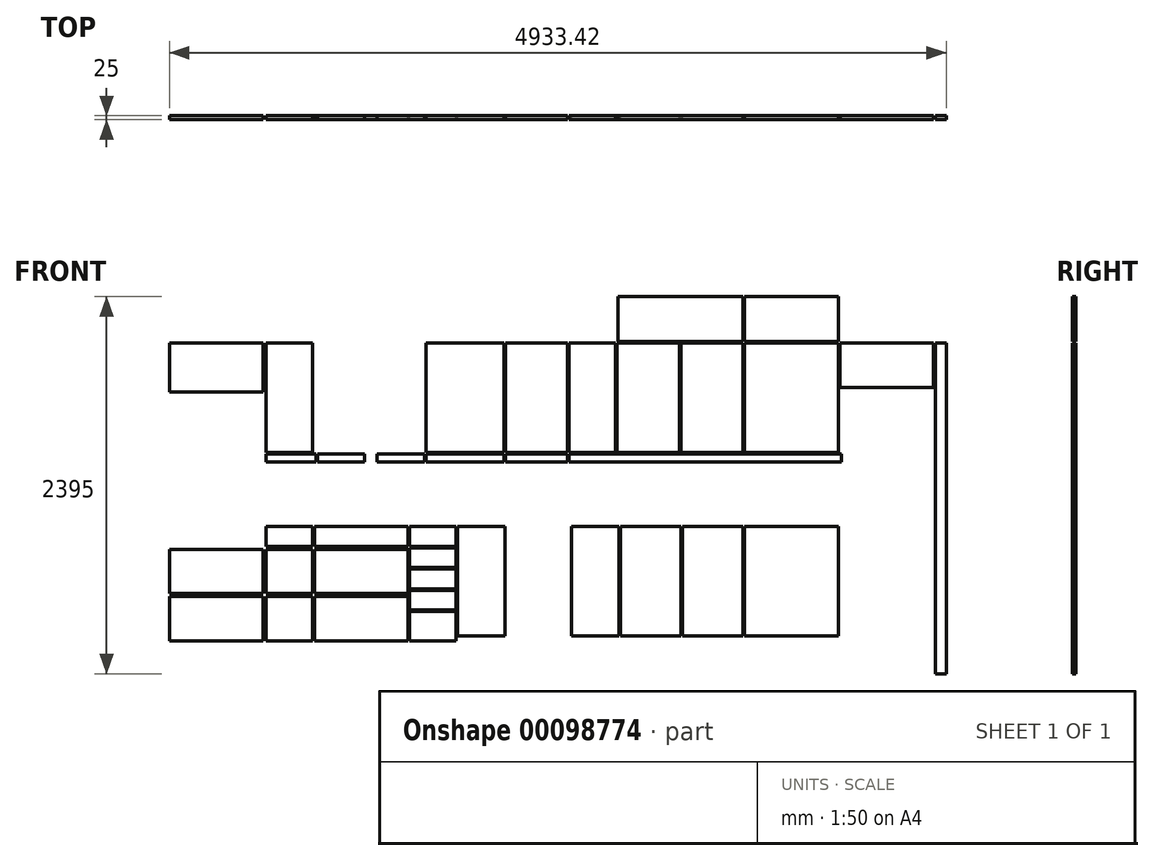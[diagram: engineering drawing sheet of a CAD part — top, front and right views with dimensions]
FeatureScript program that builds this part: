
annotation { "Feature Type Name" : "Feature", "Feature Type Description" : "" }
export const myFeature = defineFeature(function(context is Context, id is Id, definition is map)
    precondition{}
    {
        {
            var Q0;
            Q0=qCreatedBy(makeId("Front.planeOp"),FACE);
            var sketch = newSketch(context, id + "F0", { "sketchPlane" : qUnion([Q0])});
            skLineSegment(sketch, "E0.bottom", {"start": v(-883.14, -290.46) * mm, "end": v(-288.14, -290.46) * mm});
            skLineSegment(sketch, "E0.top", {"start": v(-883.14, -600.46) * mm, "end": v(-288.14, -600.46) * mm});
            skLineSegment(sketch, "E0.left", {"start": v(-883.14, -290.46) * mm, "end": v(-883.14, -600.46) * mm});
            skLineSegment(sketch, "E0.right", {"start": v(-288.14, -290.46) * mm, "end": v(-288.14, -600.46) * mm});
            skLineSegment(sketch, "E1.bottom", {"start": v(-883.14, -1600.46) * mm, "end": v(-288.14, -1600.46) * mm});
            skLineSegment(sketch, "E1.top", {"start": v(-883.14, -1880.46) * mm, "end": v(-288.14, -1880.46) * mm});
            skLineSegment(sketch, "E1.left", {"start": v(-883.14, -1600.46) * mm, "end": v(-883.14, -1880.46) * mm});
            skLineSegment(sketch, "E1.right", {"start": v(-288.14, -1600.46) * mm, "end": v(-288.14, -1880.46) * mm});
            skLineSegment(sketch, "E2.bottom", {"start": v(-883.14, -1900.46) * mm, "end": v(-288.14, -1900.46) * mm});
            skLineSegment(sketch, "E2.top", {"start": v(-883.14, -2180.46) * mm, "end": v(-288.14, -2180.46) * mm});
            skLineSegment(sketch, "E2.left", {"start": v(-883.14, -1900.46) * mm, "end": v(-883.14, -2180.46) * mm});
            skLineSegment(sketch, "E2.right", {"start": v(-288.14, -1900.46) * mm, "end": v(-288.14, -2180.46) * mm});
            skLineSegment(sketch, "E3.bottom", {"start": v(-268.14, -290.46) * mm, "end": v(26.86, -290.46) * mm});
            skLineSegment(sketch, "E3.top", {"start": v(-268.14, -985.46) * mm, "end": v(26.86, -985.46) * mm});
            skLineSegment(sketch, "E3.left", {"start": v(-268.14, -290.46) * mm, "end": v(-268.14, -985.46) * mm});
            skLineSegment(sketch, "E3.right", {"start": v(26.86, -290.46) * mm, "end": v(26.86, -985.46) * mm});
            skPoint(sketch, "E4.oppositeSnap0", {"position": v(-585.64, -1880.46) * mm});
            skLineSegment(sketch, "E4.bottom", {"start": v(-268.14, -1600.46) * mm, "end": v(26.86, -1600.46) * mm});
            skLineSegment(sketch, "E4.top", {"start": v(-268.14, -1880.46) * mm, "end": v(26.86, -1880.46) * mm});
            skLineSegment(sketch, "E4.left", {"start": v(-268.14, -1600.46) * mm, "end": v(-268.14, -1880.46) * mm});
            skLineSegment(sketch, "E4.right", {"start": v(26.86, -1600.46) * mm, "end": v(26.86, -1880.46) * mm});
            skLineSegment(sketch, "E5.bottom", {"start": v(-268.14, -1900.46) * mm, "end": v(26.86, -1900.46) * mm});
            skLineSegment(sketch, "E5.top", {"start": v(-268.14, -2180.46) * mm, "end": v(26.86, -2180.46) * mm});
            skLineSegment(sketch, "E5.left", {"start": v(-268.14, -1900.46) * mm, "end": v(-268.14, -2180.46) * mm});
            skLineSegment(sketch, "E5.right", {"start": v(26.86, -1900.46) * mm, "end": v(26.86, -2180.46) * mm});
            skLineSegment(sketch, "E6.bottom", {"start": v(-268.14, -1580.46) * mm, "end": v(26.86, -1580.46) * mm});
            skLineSegment(sketch, "E6.top", {"start": v(-268.14, -1455.46) * mm, "end": v(26.86, -1455.46) * mm});
            skLineSegment(sketch, "E6.left", {"start": v(-268.14, -1580.46) * mm, "end": v(-268.14, -1455.46) * mm});
            skLineSegment(sketch, "E6.right", {"start": v(26.86, -1580.46) * mm, "end": v(26.86, -1455.46) * mm});
            skLineSegment(sketch, "E7.bottom", {"start": v(36.86, -1455.46) * mm, "end": v(631.86, -1455.46) * mm});
            skLineSegment(sketch, "E7.top", {"start": v(36.86, -1580.46) * mm, "end": v(631.86, -1580.46) * mm});
            skLineSegment(sketch, "E7.left", {"start": v(36.86, -1455.46) * mm, "end": v(36.86, -1580.46) * mm});
            skLineSegment(sketch, "E7.right", {"start": v(631.86, -1455.46) * mm, "end": v(631.86, -1580.46) * mm});
            skLineSegment(sketch, "E8.bottom", {"start": v(36.86, -1600.46) * mm, "end": v(631.86, -1600.46) * mm});
            skLineSegment(sketch, "E8.top", {"start": v(36.86, -1880.46) * mm, "end": v(631.86, -1880.46) * mm});
            skLineSegment(sketch, "E8.left", {"start": v(36.86, -1600.46) * mm, "end": v(36.86, -1880.46) * mm});
            skLineSegment(sketch, "E8.right", {"start": v(631.86, -1600.46) * mm, "end": v(631.86, -1880.46) * mm});
            skLineSegment(sketch, "E9.bottom", {"start": v(36.86, -1900.46) * mm, "end": v(631.86, -1900.46) * mm});
            skLineSegment(sketch, "E9.top", {"start": v(36.86, -2180.46) * mm, "end": v(631.86, -2180.46) * mm});
            skLineSegment(sketch, "E9.left", {"start": v(36.86, -1900.46) * mm, "end": v(36.86, -2180.46) * mm});
            skLineSegment(sketch, "E9.right", {"start": v(631.86, -1900.46) * mm, "end": v(631.86, -2180.46) * mm});
            skLineSegment(sketch, "E10.bottom", {"start": v(56.86, -995.46) * mm, "end": v(356.86, -995.46) * mm});
            skLineSegment(sketch, "E10.top", {"start": v(56.86, -1045.46) * mm, "end": v(356.86, -1045.46) * mm});
            skLineSegment(sketch, "E10.left", {"start": v(56.86, -995.46) * mm, "end": v(56.86, -1045.46) * mm});
            skLineSegment(sketch, "E10.right", {"start": v(356.86, -995.46) * mm, "end": v(356.86, -1045.46) * mm});
            skLineSegment(sketch, "E11.bottom", {"start": v(-268.14, -995.46) * mm, "end": v(46.86, -995.46) * mm});
            skLineSegment(sketch, "E11.top", {"start": v(-268.14, -1045.46) * mm, "end": v(46.86, -1045.46) * mm});
            skLineSegment(sketch, "E11.left", {"start": v(-268.14, -995.46) * mm, "end": v(-268.14, -1045.46) * mm});
            skLineSegment(sketch, "E11.right", {"start": v(46.86, -995.46) * mm, "end": v(46.86, -1045.46) * mm});
            skLineSegment(sketch, "E12.bottom", {"start": v(641.86, -1455.46) * mm, "end": v(936.86, -1455.46) * mm});
            skLineSegment(sketch, "E12.top", {"start": v(641.86, -1580.46) * mm, "end": v(936.86, -1580.46) * mm});
            skLineSegment(sketch, "E12.left", {"start": v(641.86, -1455.46) * mm, "end": v(641.86, -1580.46) * mm});
            skLineSegment(sketch, "E12.right", {"start": v(936.86, -1455.46) * mm, "end": v(936.86, -1580.46) * mm});
            skLineSegment(sketch, "E13.bottom", {"start": v(641.86, -1725.46) * mm, "end": v(936.86, -1725.46) * mm});
            skLineSegment(sketch, "E13.top", {"start": v(641.86, -1850.46) * mm, "end": v(936.86, -1850.46) * mm});
            skLineSegment(sketch, "E13.left", {"start": v(641.86, -1725.46) * mm, "end": v(641.86, -1850.46) * mm});
            skLineSegment(sketch, "E13.right", {"start": v(936.86, -1725.46) * mm, "end": v(936.86, -1850.46) * mm});
            skLineSegment(sketch, "E14.bottom", {"start": v(641.86, -1860.46) * mm, "end": v(936.86, -1860.46) * mm});
            skLineSegment(sketch, "E14.top", {"start": v(641.86, -1985.46) * mm, "end": v(936.86, -1985.46) * mm});
            skLineSegment(sketch, "E14.left", {"start": v(641.86, -1860.46) * mm, "end": v(641.86, -1985.46) * mm});
            skLineSegment(sketch, "E14.right", {"start": v(936.86, -1860.46) * mm, "end": v(936.86, -1985.46) * mm});
            skLineSegment(sketch, "E15.bottom", {"start": v(641.86, -1995.46) * mm, "end": v(936.86, -1995.46) * mm});
            skLineSegment(sketch, "E15.top", {"start": v(641.86, -2180.46) * mm, "end": v(936.86, -2180.46) * mm});
            skLineSegment(sketch, "E15.left", {"start": v(641.86, -1995.46) * mm, "end": v(641.86, -2180.46) * mm});
            skLineSegment(sketch, "E15.right", {"start": v(936.86, -1995.46) * mm, "end": v(936.86, -2180.46) * mm});
            skLineSegment(sketch, "E16.bottom", {"start": v(641.86, -1590.46) * mm, "end": v(936.86, -1590.46) * mm});
            skLineSegment(sketch, "E16.top", {"start": v(641.86, -1715.46) * mm, "end": v(936.86, -1715.46) * mm});
            skLineSegment(sketch, "E16.left", {"start": v(641.86, -1590.46) * mm, "end": v(641.86, -1715.46) * mm});
            skLineSegment(sketch, "E16.right", {"start": v(936.86, -1590.46) * mm, "end": v(936.86, -1715.46) * mm});
            skLineSegment(sketch, "E17.bottom", {"start": v(1240.28, -290.46) * mm, "end": v(745.28, -290.46) * mm});
            skLineSegment(sketch, "E17.top", {"start": v(1240.28, -985.46) * mm, "end": v(745.28, -985.46) * mm});
            skLineSegment(sketch, "E17.left", {"start": v(1240.28, -290.46) * mm, "end": v(1240.28, -985.46) * mm});
            skLineSegment(sketch, "E17.right", {"start": v(745.28, -290.46) * mm, "end": v(745.28, -985.46) * mm});
            skPoint(sketch, "E18.firstSnap0", {"position": v(1240.28, -637.96) * mm});
            skLineSegment(sketch, "E18.bottom", {"start": v(1240.28, -1045.46) * mm, "end": v(745.28, -1045.46) * mm});
            skLineSegment(sketch, "E18.top", {"start": v(1240.28, -995.46) * mm, "end": v(745.28, -995.46) * mm});
            skLineSegment(sketch, "E18.left", {"start": v(1240.28, -1045.46) * mm, "end": v(1240.28, -995.46) * mm});
            skLineSegment(sketch, "E18.right", {"start": v(745.28, -1045.46) * mm, "end": v(745.28, -995.46) * mm});
            skLineSegment(sketch, "E19.bottom", {"start": v(735.28, -1045.46) * mm, "end": v(435.28, -1045.46) * mm});
            skLineSegment(sketch, "E19.top", {"start": v(735.28, -995.46) * mm, "end": v(435.28, -995.46) * mm});
            skLineSegment(sketch, "E19.left", {"start": v(735.28, -1045.46) * mm, "end": v(735.28, -995.46) * mm});
            skLineSegment(sketch, "E19.right", {"start": v(435.28, -1045.46) * mm, "end": v(435.28, -995.46) * mm});
            skLineSegment(sketch, "E20.bottom", {"start": v(1250.28, -985.46) * mm, "end": v(1645.28, -985.46) * mm});
            skLineSegment(sketch, "E20.top", {"start": v(1250.28, -290.46) * mm, "end": v(1645.28, -290.46) * mm});
            skLineSegment(sketch, "E20.left", {"start": v(1250.28, -985.46) * mm, "end": v(1250.28, -290.46) * mm});
            skLineSegment(sketch, "E20.right", {"start": v(1645.28, -985.46) * mm, "end": v(1645.28, -290.46) * mm});
            skLineSegment(sketch, "E21.bottom", {"start": v(1250.28, -995.46) * mm, "end": v(1645.28, -995.46) * mm});
            skLineSegment(sketch, "E21.top", {"start": v(1250.28, -1045.46) * mm, "end": v(1645.28, -1045.46) * mm});
            skLineSegment(sketch, "E21.left", {"start": v(1250.28, -995.46) * mm, "end": v(1250.28, -1045.46) * mm});
            skLineSegment(sketch, "E21.right", {"start": v(1645.28, -995.46) * mm, "end": v(1645.28, -1045.46) * mm});
            skLineSegment(sketch, "E22.bottom", {"start": v(946.86, -1455.46) * mm, "end": v(1246.86, -1455.46) * mm});
            skLineSegment(sketch, "E22.top", {"start": v(946.86, -2150.46) * mm, "end": v(1246.86, -2150.46) * mm});
            skLineSegment(sketch, "E22.left", {"start": v(946.86, -1455.46) * mm, "end": v(946.86, -2150.46) * mm});
            skLineSegment(sketch, "E22.right", {"start": v(1246.86, -1455.46) * mm, "end": v(1246.86, -2150.46) * mm});
            skSolve(sketch);
        }
        {
            var Q0;
            Q0=qCreatedBy(makeId("Front.planeOp"),FACE);
            var sketch = newSketch(context, id + "F1", { "sketchPlane" : qUnion([Q0])});
            skLineSegment(sketch, "E23.bottom", {"start": v(1655.28, -290.46) * mm, "end": v(1950.28, -290.46) * mm});
            skLineSegment(sketch, "E23.top", {"start": v(1655.28, -985.46) * mm, "end": v(1950.28, -985.46) * mm});
            skLineSegment(sketch, "E23.left", {"start": v(1655.28, -290.46) * mm, "end": v(1655.28, -985.46) * mm});
            skLineSegment(sketch, "E23.right", {"start": v(1950.28, -290.46) * mm, "end": v(1950.28, -985.46) * mm});
            skLineSegment(sketch, "E24.bottom", {"start": v(1960.28, -290.46) * mm, "end": v(2355.28, -290.46) * mm});
            skLineSegment(sketch, "E24.top", {"start": v(1960.28, -985.46) * mm, "end": v(2355.28, -985.46) * mm});
            skLineSegment(sketch, "E24.left", {"start": v(1960.28, -290.46) * mm, "end": v(1960.28, -985.46) * mm});
            skLineSegment(sketch, "E24.right", {"start": v(2355.28, -290.46) * mm, "end": v(2355.28, -985.46) * mm});
            skLineSegment(sketch, "E25.bottom", {"start": v(2365.28, -290.46) * mm, "end": v(2760.28, -290.46) * mm});
            skLineSegment(sketch, "E25.top", {"start": v(2365.28, -985.46) * mm, "end": v(2760.28, -985.46) * mm});
            skLineSegment(sketch, "E25.left", {"start": v(2365.28, -290.46) * mm, "end": v(2365.28, -985.46) * mm});
            skLineSegment(sketch, "E25.right", {"start": v(2760.28, -290.46) * mm, "end": v(2760.28, -985.46) * mm});
            skLineSegment(sketch, "E26.bottom", {"start": v(2770.28, -290.46) * mm, "end": v(3365.28, -290.46) * mm});
            skLineSegment(sketch, "E26.top", {"start": v(2770.28, -985.46) * mm, "end": v(3365.28, -985.46) * mm});
            skLineSegment(sketch, "E26.left", {"start": v(2770.28, -290.46) * mm, "end": v(2770.28, -985.46) * mm});
            skLineSegment(sketch, "E26.right", {"start": v(3365.28, -290.46) * mm, "end": v(3365.28, -985.46) * mm});
            skLineSegment(sketch, "E27.bottom", {"start": v(3375.28, -290.46) * mm, "end": v(3970.28, -290.46) * mm});
            skLineSegment(sketch, "E27.top", {"start": v(3375.28, -570.46) * mm, "end": v(3970.28, -570.46) * mm});
            skLineSegment(sketch, "E27.left", {"start": v(3375.28, -290.46) * mm, "end": v(3375.28, -570.46) * mm});
            skLineSegment(sketch, "E27.right", {"start": v(3970.28, -290.46) * mm, "end": v(3970.28, -570.46) * mm});
            skLineSegment(sketch, "E28.bottom", {"start": v(3365.28, -280.46) * mm, "end": v(2770.28, -280.46) * mm});
            skLineSegment(sketch, "E28.top", {"start": v(3365.28, 4.54) * mm, "end": v(2770.28, 4.54) * mm});
            skLineSegment(sketch, "E28.left", {"start": v(3365.28, -280.46) * mm, "end": v(3365.28, 4.54) * mm});
            skLineSegment(sketch, "E28.right", {"start": v(2770.28, -280.46) * mm, "end": v(2770.28, 4.54) * mm});
            skLineSegment(sketch, "E29.bottom", {"start": v(2760.28, -280.46) * mm, "end": v(1965.28, -280.46) * mm});
            skLineSegment(sketch, "E29.top", {"start": v(2760.28, 4.54) * mm, "end": v(1965.28, 4.54) * mm});
            skLineSegment(sketch, "E29.left", {"start": v(2760.28, -280.46) * mm, "end": v(2760.28, 4.54) * mm});
            skLineSegment(sketch, "E29.right", {"start": v(1965.28, -280.46) * mm, "end": v(1965.28, 4.54) * mm});
            skLineSegment(sketch, "E30.bottom", {"start": v(3980.28, -290.46) * mm, "end": v(4050.28, -290.46) * mm});
            skLineSegment(sketch, "E30.top", {"start": v(3980.28, -2390.46) * mm, "end": v(4050.28, -2390.46) * mm});
            skLineSegment(sketch, "E30.left", {"start": v(3980.28, -290.46) * mm, "end": v(3980.28, -2390.46) * mm});
            skLineSegment(sketch, "E30.right", {"start": v(4050.28, -290.46) * mm, "end": v(4050.28, -2390.46) * mm});
            skLineSegment(sketch, "E31.bottom", {"start": v(1655.28, -995.46) * mm, "end": v(3385.28, -995.46) * mm});
            skLineSegment(sketch, "E31.top", {"start": v(1655.28, -1045.46) * mm, "end": v(3385.28, -1045.46) * mm});
            skLineSegment(sketch, "E31.left", {"start": v(1655.28, -995.46) * mm, "end": v(1655.28, -1045.46) * mm});
            skLineSegment(sketch, "E31.right", {"start": v(3385.28, -995.46) * mm, "end": v(3385.28, -1045.46) * mm});
            skLineSegment(sketch, "E32.bottom", {"start": v(1670.28, -1455.46) * mm, "end": v(1970.28, -1455.46) * mm});
            skLineSegment(sketch, "E32.top", {"start": v(1670.28, -2150.46) * mm, "end": v(1970.28, -2150.46) * mm});
            skLineSegment(sketch, "E32.left", {"start": v(1670.28, -1455.46) * mm, "end": v(1670.28, -2150.46) * mm});
            skLineSegment(sketch, "E32.right", {"start": v(1970.28, -1455.46) * mm, "end": v(1970.28, -2150.46) * mm});
            skLineSegment(sketch, "E33.bottom", {"start": v(1980.28, -1455.46) * mm, "end": v(2365.28, -1455.46) * mm});
            skLineSegment(sketch, "E33.top", {"start": v(1980.28, -2150.46) * mm, "end": v(2365.28, -2150.46) * mm});
            skLineSegment(sketch, "E33.left", {"start": v(1980.28, -1455.46) * mm, "end": v(1980.28, -2150.46) * mm});
            skLineSegment(sketch, "E33.right", {"start": v(2365.28, -1455.46) * mm, "end": v(2365.28, -2150.46) * mm});
            skLineSegment(sketch, "E34.bottom", {"start": v(2375.28, -1455.46) * mm, "end": v(2760.28, -1455.46) * mm});
            skLineSegment(sketch, "E34.top", {"start": v(2375.28, -2150.46) * mm, "end": v(2760.28, -2150.46) * mm});
            skLineSegment(sketch, "E34.left", {"start": v(2375.28, -1455.46) * mm, "end": v(2375.28, -2150.46) * mm});
            skLineSegment(sketch, "E34.right", {"start": v(2760.28, -1455.46) * mm, "end": v(2760.28, -2150.46) * mm});
            skLineSegment(sketch, "E35.bottom", {"start": v(2770.28, -1455.46) * mm, "end": v(3365.28, -1455.46) * mm});
            skLineSegment(sketch, "E35.top", {"start": v(2770.28, -2150.46) * mm, "end": v(3365.28, -2150.46) * mm});
            skLineSegment(sketch, "E35.left", {"start": v(2770.28, -1455.46) * mm, "end": v(2770.28, -2150.46) * mm});
            skLineSegment(sketch, "E35.right", {"start": v(3365.28, -1455.46) * mm, "end": v(3365.28, -2150.46) * mm});
            skSolve(sketch);
        }
        {
            var Q0;
            Q0 = qSketchRegion(id + "F1", true);
            var Q1;
            Q1 = qSketchRegion(id + "F0", true);
            extrude(context, id + "F2", {"entities" : qUnion([Q0, Q1]), "depth" : 25 * mm});
        }
    });
